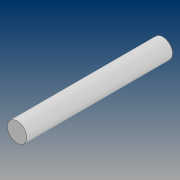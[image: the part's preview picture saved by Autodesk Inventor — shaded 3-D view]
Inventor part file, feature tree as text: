
AUTODESK INVENTOR PART (.ipt)
format: ipt  version: 2021 (Build 250183000, 183)  size: 75,264 bytes
history: native  units: mm
features: extrude x1, sketch x1
ambient origin geometry x8: Origin, YZ Plane, XZ Plane, XY Plane, X Axis, Y Axis, Z Axis, Center Point
bodies: Solid1 (feature_tree)
feature tree (2):
  extrude  "Extrusion1"  Depth=60.0mm TaperAngle=0.0deg
  sketch  "Sketch1"  dims[d0=8.0mm d1=60.0mm d2=0.0mm]
